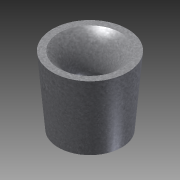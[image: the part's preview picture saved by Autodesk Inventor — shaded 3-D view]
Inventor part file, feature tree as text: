
AUTODESK INVENTOR PART (.ipt)
format: ipt  version: 2015 (Build 190159000, 159)  size: 176,640 bytes
history: native  units: in
note: dims shown in document units (in); Inventor stores cm internally (conversion verified against a paired STEP export)
features: revolve x1, sketch x1
ambient origin geometry x8: Origin, YZ Plane, XZ Plane, XY Plane, X Axis, Y Axis, Z Axis, Center Point
bodies: Solid1 (feature_tree)
feature tree (2):
  revolve  "Revolution1"  [1 undecoded]
  sketch  "Sketch1"  dims[d25=90.0deg d26=0.75in d27=1.0in d28=0.2185in d29=2.594in d30=0.5841in d31=0.5in d32=0.5in d33=1.75in d34=0.25in d35=105.0deg d36=0.5in d37=0.5in d38=0.25in d39=0.375in d40=2.0in d41=0.5in d42=0.25in d43=0.234in d44=0.25in d45=2.0in d46=0.25in d47=105.0deg d48=0.125in d49=0.25in d50=2.3995in d51=0.125in d52=0.25in d53=1.0in d54=1.6531in d55=0.1443in]
note: 1 required parameter value undecoded (feature->parameter linkage not recoverable at this tier; creation-order binding heuristic only, values carry confidence <= 0.55)
